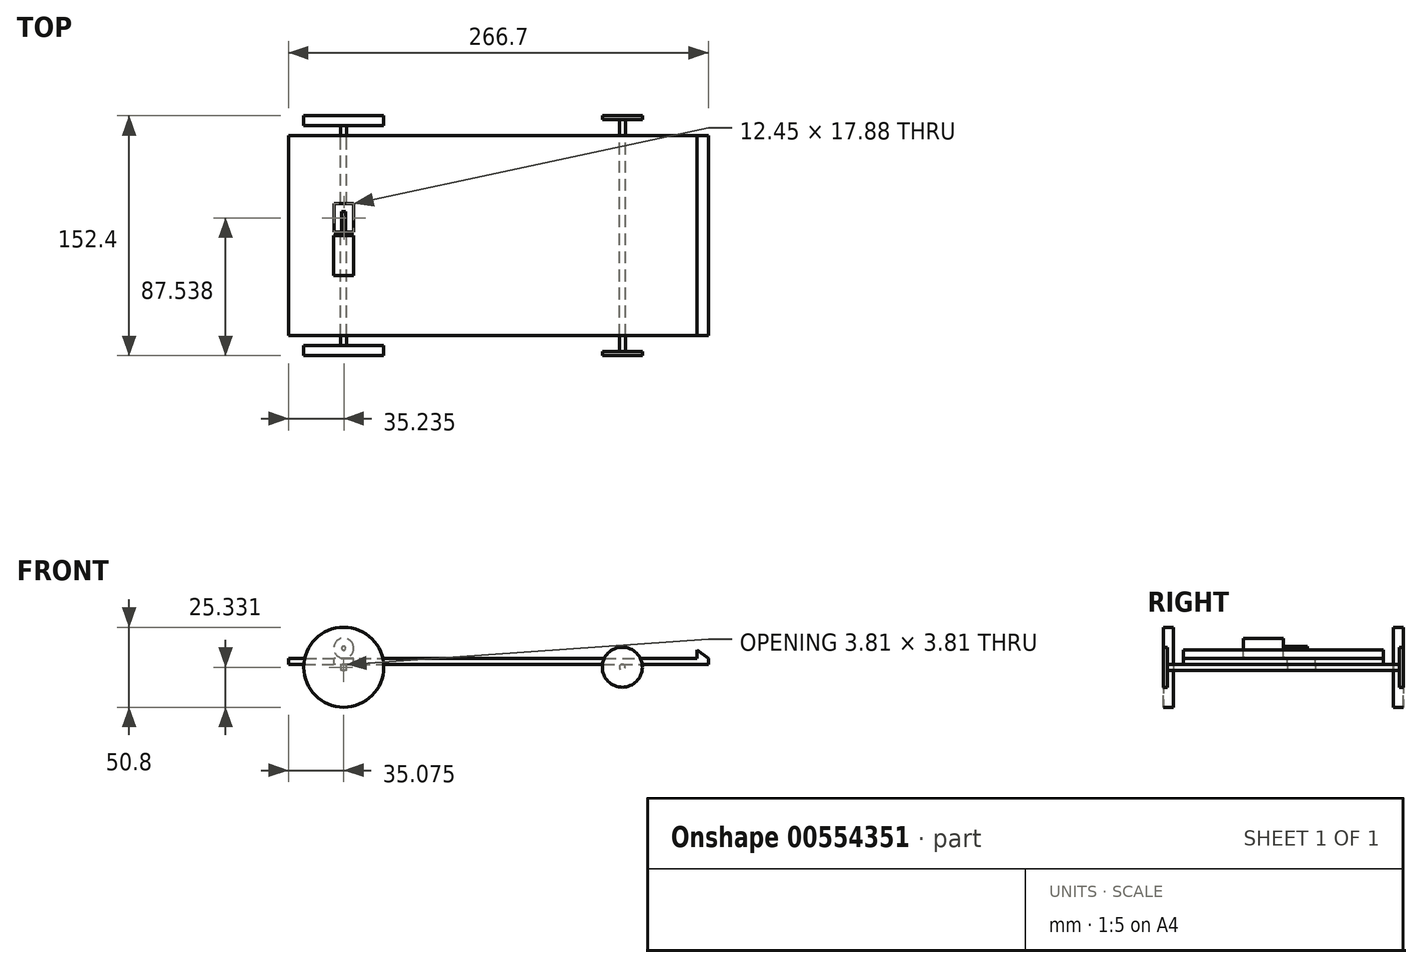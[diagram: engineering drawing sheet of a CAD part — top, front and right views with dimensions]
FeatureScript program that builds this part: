
annotation { "Feature Type Name" : "Feature", "Feature Type Description" : "" }
export const myFeature = defineFeature(function(context is Context, id is Id, definition is map)
    precondition{}
    {
        {
            var Q0;
            Q0=qCreatedBy(makeId("Front.planeOp"),FACE);
            var sketch = newSketch(context, id + "F0", { "sketchPlane" : qUnion([Q0])});
            skLineSegment(sketch, "E0.bottom", {"start": v(-76.22, -2.37) * mm, "end": v(190.48, -2.37) * mm});
            skLineSegment(sketch, "E0.top", {"start": v(-76.22, 1.44) * mm, "end": v(190.48, 1.44) * mm});
            skLineSegment(sketch, "E0.left", {"start": v(-76.22, -2.37) * mm, "end": v(-76.22, 1.44) * mm});
            skLineSegment(sketch, "E0.right", {"start": v(190.48, -2.37) * mm, "end": v(190.48, 1.44) * mm});
            skLineSegment(sketch, "E1.bottom", {"start": v(-34.76, 1.44) * mm, "end": v(-30.95, 1.44) * mm});
            skLineSegment(sketch, "E1.top", {"start": v(-34.76, 26.84) * mm, "end": v(-30.95, 26.84) * mm});
            skLineSegment(sketch, "E1.left", {"start": v(-34.76, 1.44) * mm, "end": v(-34.76, 26.84) * mm});
            skLineSegment(sketch, "E1.right", {"start": v(-30.95, 1.44) * mm, "end": v(-30.95, 26.84) * mm});
            skCircle(sketch, "E2", {"center": v(-41.15, -4.28) * mm, "radius": 1.9 * mm});
            skCircle(sketch, "E3", {"center": v(135.8, -4.28) * mm, "radius": 1.9 * mm});
            skLineSegment(sketch, "E4", {"start": v(183.38, 1.44) * mm, "end": v(183.38, 6.84) * mm});
            skLineSegment(sketch, "E5", {"start": v(183.38, 6.84) * mm, "end": v(190.48, 1.44) * mm});
            skCircle(sketch, "E6", {"center": v(-41.15, 7.85) * mm, "radius": 6.35 * mm});
            skCircle(sketch, "E7", {"center": v(-41.15, 7.85) * mm, "radius": 1.27 * mm});
            skSolve(sketch);
        }
        {
            var Q0;
            Q0=makeQuery(id+"F0.imprint","IMPRINT",FACE,{"disambiguationData":[TD([[makeQuery(id+"F0.imprint","IMPRINT",EDGE,{"derivedFrom":sQuery(id+"F0.wireOp",EDGE,"E0.bottom")}),1.0]])]});
            var Q1;
            Q1=makeQuery(id+"F0.imprint","IMPRINT",FACE,{"disambiguationData":[TD([[makeQuery(id+"F0.imprint","IMPRINT",EDGE,{"derivedFrom":sQuery(id+"F0.wireOp",EDGE,"E1.bottom")}),1.0]])]});
            extrude(context, id + "F1", {"entities" : qUnion([Q0, Q1]), "endBound" : BoundingType.SYMMETRIC, "depth" : 127 * mm, "offsetDistance" : 25.4 * mm});
        }
        {
            var Q0;
            Q0=makeQuery(id+"F0.imprint","IMPRINT",FACE,{"disambiguationData":[TD([[makeQuery(id+"F0.imprint","IMPRINT",EDGE,{"derivedFrom":sQuery(id+"F0.wireOp",EDGE,"E2")}),1.0]])]});
            var Q1;
            Q1=makeQuery(id+"F0.imprint","IMPRINT",FACE,{"disambiguationData":[TD([[makeQuery(id+"F0.imprint","IMPRINT",EDGE,{"derivedFrom":sQuery(id+"F0.wireOp",EDGE,"E3")}),1.0]])]});
            extrude(context, id + "F2", {"entities" : qUnion([Q0, Q1]), "endBound" : BoundingType.SYMMETRIC, "depth" : 152.4 * mm, "offsetDistance" : 25.4 * mm});
        }
        {
            var Q0;
            Q0=qCreatedBy(makeId("Front.planeOp"),FACE);
            var sketch = newSketch(context, id + "F3", { "sketchPlane" : qUnion([Q0])});
            skCircle(sketch, "E8", {"center": v(-41.13, -4.21) * mm, "radius": 25.4 * mm});
            skCircle(sketch, "E9", {"center": v(135.83, -4.21) * mm, "radius": 12.7 * mm});
            skSolve(sketch);
        }
        {
            var Q0;
            Q0=makeQuery(id+"F3.imprint","IMPRINT",FACE,{"disambiguationData":[TD([[makeQuery(id+"F3.imprint","IMPRINT",EDGE,{"derivedFrom":sQuery(id+"F3.wireOp",EDGE,"E8")}),1.0]])]});
            extrude(context, id + "F4", {"entities" : qUnion([Q0]), "operationType" : NewBodyOperationType.ADD, "depth" : 76.2 * mm, "offsetDistance" : 25.4 * mm, "hasSecondDirection" : true, "secondDirectionOppositeDirection" : false, "secondDirectionDepth" : 69.85 * mm});
        }
        {
            var Q0;
            Q0=makeQuery(id+"F3.imprint","IMPRINT",FACE,{"disambiguationData":[TD([[makeQuery(id+"F3.imprint","IMPRINT",EDGE,{"derivedFrom":sQuery(id+"F3.wireOp",EDGE,"E9")}),1.0]])]});
            extrude(context, id + "F5", {"entities" : qUnion([Q0]), "operationType" : NewBodyOperationType.ADD, "depth" : 76.2 * mm, "offsetDistance" : 25.4 * mm, "hasSecondDirection" : true, "secondDirectionOppositeDirection" : false, "secondDirectionDepth" : 73.66 * mm});
        }
        {
            var Q0;
            Q0=makeQuery(id+"F3.imprint","IMPRINT",FACE,{"disambiguationData":[TD([[makeQuery(id+"F3.imprint","IMPRINT",EDGE,{"derivedFrom":sQuery(id+"F3.wireOp",EDGE,"E9")}),1.0]])]});
            extrude(context, id + "F6", {"entities" : qUnion([Q0]), "operationType" : NewBodyOperationType.ADD, "oppositeDirection" : true, "depth" : 76.2 * mm, "offsetDistance" : 25.4 * mm, "hasSecondDirection" : true, "secondDirectionOppositeDirection" : true, "secondDirectionDepth" : 73.66 * mm});
        }
        {
            var Q0;
            Q0=makeQuery(id+"F3.imprint","IMPRINT",FACE,{"disambiguationData":[TD([[makeQuery(id+"F3.imprint","IMPRINT",EDGE,{"derivedFrom":sQuery(id+"F3.wireOp",EDGE,"E8")}),1.0]])]});
            extrude(context, id + "F7", {"entities" : qUnion([Q0]), "operationType" : NewBodyOperationType.ADD, "oppositeDirection" : true, "depth" : 76.2 * mm, "offsetDistance" : 25.4 * mm, "hasSecondDirection" : true, "secondDirectionOppositeDirection" : true, "secondDirectionDepth" : 69.85 * mm});
        }
        {
            var Q0;
            {var subQ2=sQuery(id+"F0.wireOp",EDGE,"E4");Q0=makeQuery(id+"F0.imprint","IMPRINT",FACE,{"disambiguationData":[TD([[makeQuery(id+"F0.imprint","IMPRINT",EDGE,{"derivedFrom":subQ2}),-1.0]])]});}
            extrude(context, id + "F8", {"entities" : qUnion([Q0]), "operationType" : NewBodyOperationType.ADD, "endBound" : BoundingType.SYMMETRIC, "depth" : 127 * mm, "offsetDistance" : 25.4 * mm});
        }
        {
            var Q0;
            {var subQ0=sQuery(id+"F0.wireOp",EDGE,"E0.top");Q0=makeQuery(id+"F1.opExtrude","SWEPT_FACE",FACE,{"disambiguationData":[OSD([subQ0]),TDD([makeQuery(id+"F0.imprint","IMPRINT",EDGE,{"disambiguationData":[TD([[makeQuery(id+"F0.imprint","INTERSECT",VERTEX,{"derivedFrom":[subQ0,sQuery(id+"F0.wireOp",EDGE,"E0.left")]}),-1.0]])],"derivedFrom":subQ0})])]});}
            var sketch = newSketch(context, id + "F9", { "sketchPlane" : qUnion([Q0])});
            skLineSegment(sketch, "E10.bottom", {"start": v(-34.76, 2.4) * mm, "end": v(-47.21, 2.4) * mm});
            skLineSegment(sketch, "E10.top", {"start": v(-34.76, 20.28) * mm, "end": v(-47.21, 20.28) * mm});
            skLineSegment(sketch, "E10.left", {"start": v(-34.76, 2.4) * mm, "end": v(-34.76, 20.28) * mm});
            skLineSegment(sketch, "E10.right", {"start": v(-47.21, 2.4) * mm, "end": v(-47.21, 20.28) * mm});
            skPoint(sketch, "E11.firstSnap0", {"position": v(-40.98, 20.28) * mm});
            skSolve(sketch);
        }
        {
            var Q0;
            Q0=makeQuery(id+"F9.imprint","IMPRINT",FACE,{"disambiguationData":[TD([[makeQuery(id+"F9.imprint","IMPRINT",EDGE,{"derivedFrom":sQuery(id+"F9.wireOp",EDGE,"E10.bottom")}),-1.0]])]});
            extrude(context, id + "F10", {"entities" : qUnion([Q0]), "operationType" : NewBodyOperationType.REMOVE, "oppositeDirection" : true, "depth" : 25.4 * mm, "offsetDistance" : 25.4 * mm});
        }
        {
            var Q0;
            Q0=makeQuery(id+"F0.imprint","IMPRINT",FACE,{"disambiguationData":[TD([[makeQuery(id+"F0.imprint","IMPRINT",EDGE,{"derivedFrom":sQuery(id+"F0.wireOp",EDGE,"E7")}),1.0]])]});
            extrude(context, id + "F11", {"entities" : qUnion([Q0]), "oppositeDirection" : true, "depth" : 15.24 * mm, "offsetDistance" : 25.4 * mm});
        }
        {
            var Q0;
            Q0=makeQuery(id+"F0.imprint","IMPRINT",FACE,{"disambiguationData":[TD([[makeQuery(id+"F0.imprint","IMPRINT",EDGE,{"derivedFrom":sQuery(id+"F0.wireOp",EDGE,"E6")}),1.0]])]});
            var Q1;
            Q1=makeQuery(id+"F0.imprint","IMPRINT",FACE,{"disambiguationData":[TD([[makeQuery(id+"F0.imprint","IMPRINT",EDGE,{"derivedFrom":sQuery(id+"F0.wireOp",EDGE,"E7")}),1.0]])]});
            extrude(context, id + "F12", {"entities" : qUnion([Q0, Q1]), "operationType" : NewBodyOperationType.ADD, "depth" : 25.4 * mm, "offsetDistance" : 25.4 * mm});
        }
    });
